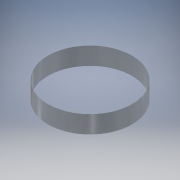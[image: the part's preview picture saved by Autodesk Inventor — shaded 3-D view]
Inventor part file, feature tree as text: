
AUTODESK INVENTOR PART (.ipt)
format: ipt  version: 2016 (Build 200138000, 138)  size: 104,448 bytes
history: native  units: in
note: dims shown in document units (in); Inventor stores cm internally (conversion verified against a paired STEP export)
features: revolve x1, sketch x1
ambient origin geometry x8: Origin, YZ Plane, XZ Plane, XY Plane, X Axis, Y Axis, Z Axis, Center Point
bodies: Solid1 (feature_tree)
feature tree (2):
  revolve  "Revolution1"  [1 undecoded]
  sketch  "Sketch1"  dims[d0=14.1732in d1=33.8583in d2=90.0deg]
note: 1 required parameter value undecoded (feature->parameter linkage not recoverable at this tier; creation-order binding heuristic only, values carry confidence <= 0.55)
